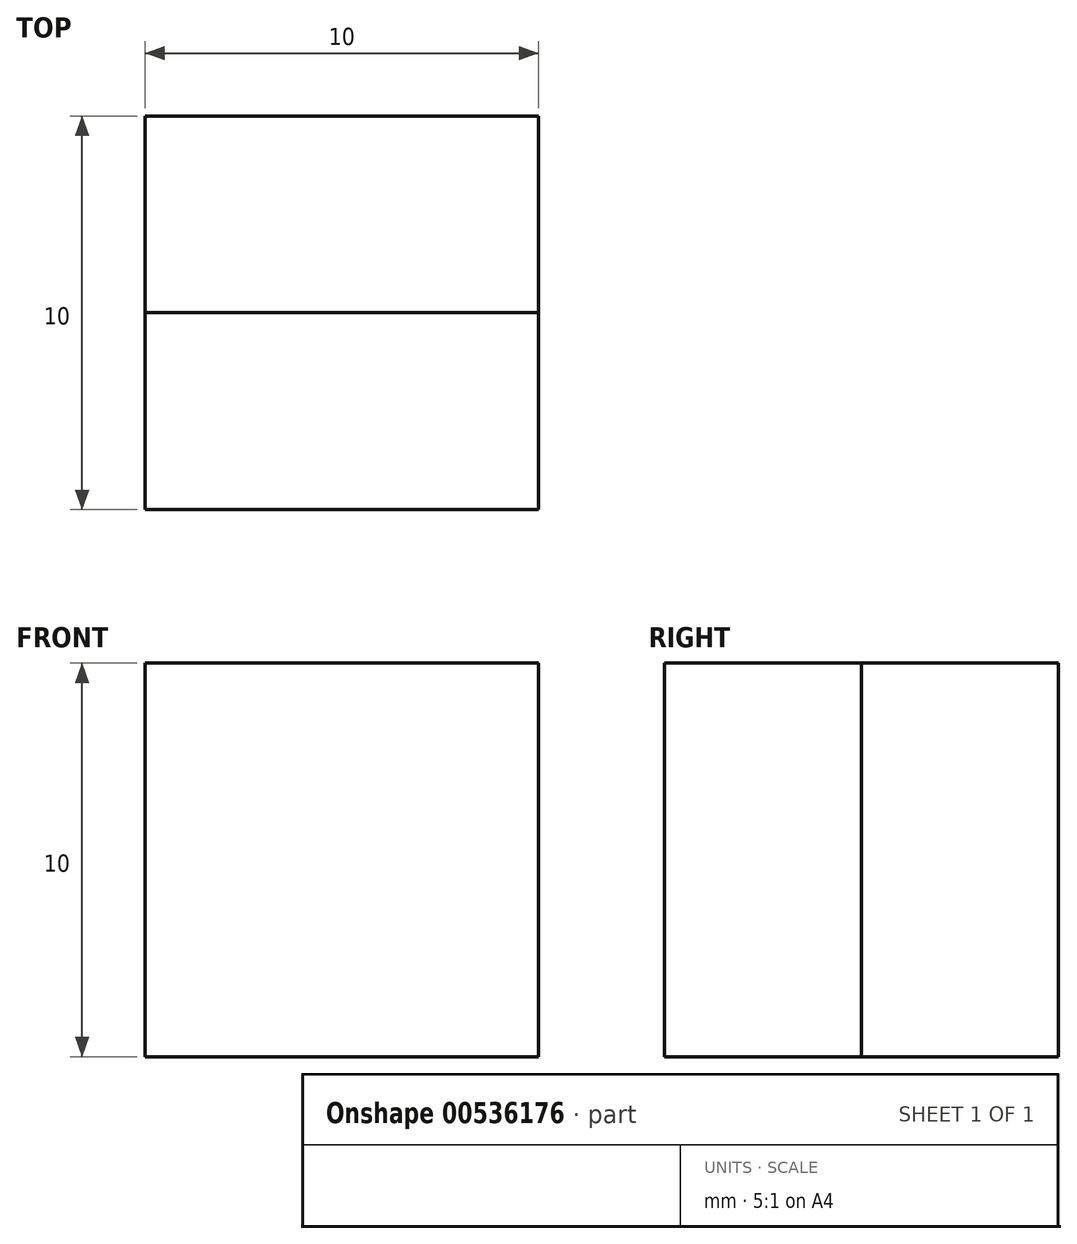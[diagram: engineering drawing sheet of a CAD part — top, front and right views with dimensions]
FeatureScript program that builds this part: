
annotation { "Feature Type Name" : "Feature", "Feature Type Description" : "" }
export const myFeature = defineFeature(function(context is Context, id is Id, definition is map)
    precondition{}
    {
        {
            var Q0;
            Q0=qCreatedBy(makeId("Front.planeOp"),FACE);
            var sketch = newSketch(context, id + "F0", { "sketchPlane" : qUnion([Q0])});
            skLineSegment(sketch, "E0.bottom", {"start": v(5, -5) * mm, "end": v(-5, -5) * mm});
            skLineSegment(sketch, "E0.top", {"start": v(5, 5) * mm, "end": v(-5, 5) * mm});
            skLineSegment(sketch, "E0.left", {"start": v(5, -5) * mm, "end": v(5, 5) * mm});
            skLineSegment(sketch, "E0.right", {"start": v(-5, -5) * mm, "end": v(-5, 5) * mm});
            skPoint(sketch, "E0.middle", {"position": v(0, 0) * mm});
            skSolve(sketch);
        }
        {
            var Q0;
            Q0=makeQuery(id+"F0.imprint","IMPRINT",FACE,{"disambiguationData":[TD([[makeQuery(id+"F0.imprint","IMPRINT",EDGE,{"derivedFrom":sQuery(id+"F0.wireOp",EDGE,"E0.bottom")}),-1.0]])]});
            extrude(context, id + "F1", {"entities" : qUnion([Q0]), "depth" : 5 * mm, "offsetDistance" : 25 * mm});
        }
        {
            var Q0;
            Q0=makeQuery(id+"F1.opExtrude","SWEPT_BODY",BODY,{"disambiguationData":[OSD([sQuery(id+"F0.wireOp",EDGE,"E0.bottom"),sQuery(id+"F0.wireOp",EDGE,"E0.top"),sQuery(id+"F0.wireOp",EDGE,"E0.left"),sQuery(id+"F0.wireOp",EDGE,"E0.right")])]});
            transform(context, id + "F2", {"entities" : qUnion([Q0]), "transformType" : TransformType.TRANSLATION_3D, "dx" : 0 * mm, "dy" : 5 * mm, "dz" : 0 * mm, "makeCopy" : true});
        }
    });
